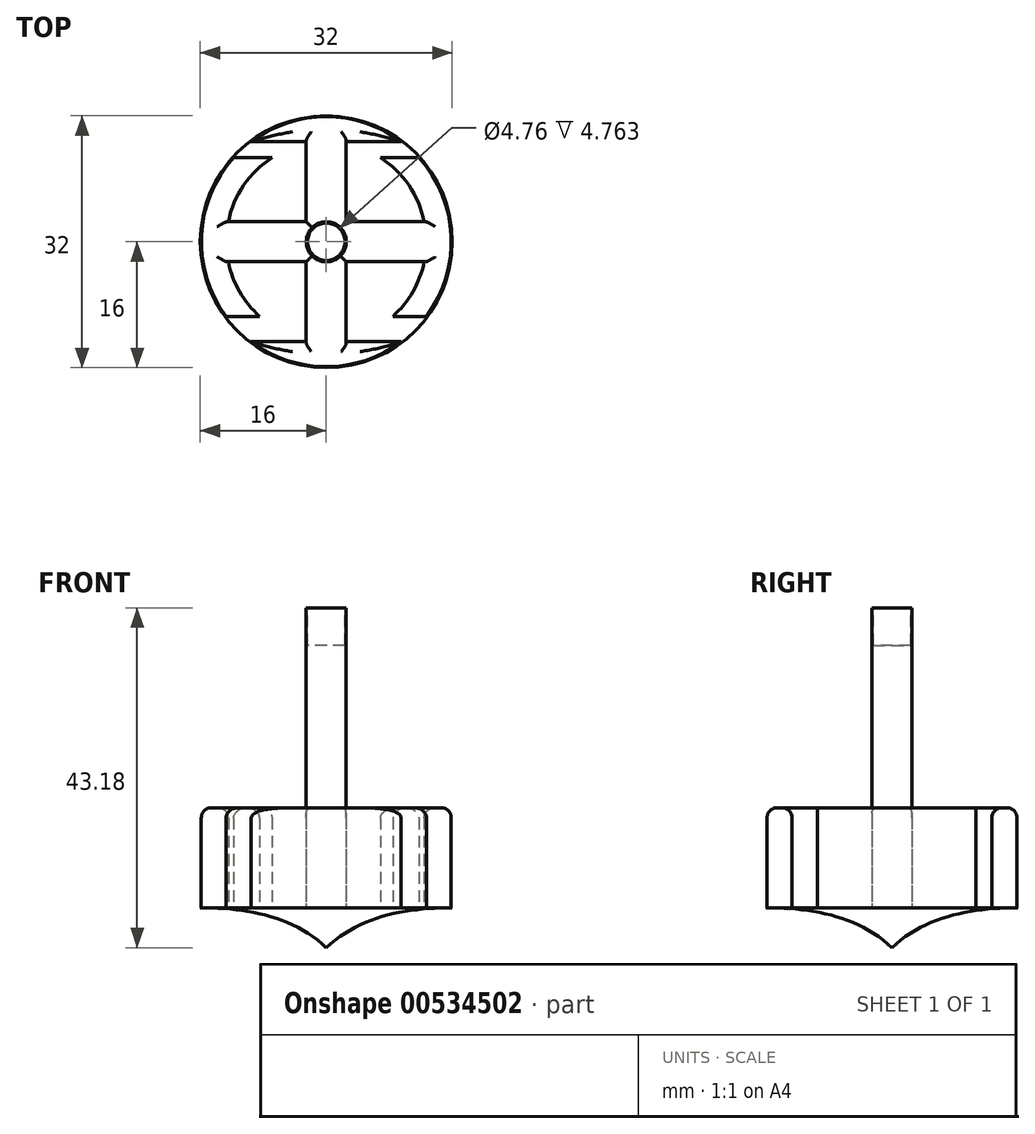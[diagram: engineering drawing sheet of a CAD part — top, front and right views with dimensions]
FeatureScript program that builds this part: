
annotation { "Feature Type Name" : "Feature", "Feature Type Description" : "" }
export const myFeature = defineFeature(function(context is Context, id is Id, definition is map)
    precondition{}
    {
        {
            var Q0;
            Q0=qCreatedBy(makeId("Top.planeOp"),FACE);
            var sketch = newSketch(context, id + "F0", { "sketchPlane" : qUnion([Q0])});
            skArc(sketch, "E0", {"start": v(-15.88, 0) * mm, "mid": v(-15.07, -5) * mm, "end": v(-12.73, -9.48) * mm});
            skArc(sketch, "E1", {"start": v(-15.88, 0) * mm, "mid": v(-14.8, 5.72) * mm, "end": v(-11.75, 10.67) * mm});
            skArc(sketch, "E2", {"start": v(15.88, 0) * mm, "mid": v(14.8, 5.72) * mm, "end": v(11.75, 10.67) * mm});
            skArc(sketch, "E3", {"start": v(15.88, 0) * mm, "mid": v(15.07, -5) * mm, "end": v(12.73, -9.48) * mm});
            skArc(sketch, "E4", {"start": v(-12.7, 0) * mm, "mid": v(-11.15, 6.08) * mm, "end": v(-6.89, 10.67) * mm});
            skArc(sketch, "E5", {"start": v(-12.7, 0) * mm, "mid": v(-11.59, -5.2) * mm, "end": v(-8.45, -9.48) * mm});
            skArc(sketch, "E6", {"start": v(12.7, 0) * mm, "mid": v(11.15, 6.08) * mm, "end": v(6.89, 10.67) * mm});
            skArc(sketch, "E7", {"start": v(12.7, 0) * mm, "mid": v(11.59, -5.2) * mm, "end": v(8.45, -9.48) * mm});
            skLineSegment(sketch, "E8", {"start": v(-11.75, 10.67) * mm, "end": v(-6.89, 10.67) * mm});
            skLineSegment(sketch, "E9", {"start": v(-8.45, -9.48) * mm, "end": v(-12.73, -9.48) * mm});
            skLineSegment(sketch, "E10", {"start": v(8.45, -9.48) * mm, "end": v(12.73, -9.48) * mm});
            skLineSegment(sketch, "E11", {"start": v(6.89, 10.67) * mm, "end": v(11.75, 10.67) * mm});
            skLineSegment(sketch, "E12", {"start": v(0, 12.7) * mm, "end": v(9.52, 12.7) * mm});
            skLineSegment(sketch, "E13", {"start": v(0, 12.7) * mm, "end": v(-9.52, 12.7) * mm});
            skArc(sketch, "E14", {"start": v(0, 15.88) * mm, "mid": v(-5.02, 15.06) * mm, "end": v(-9.52, 12.7) * mm});
            skArc(sketch, "E15", {"start": v(0, 15.88) * mm, "mid": v(5.02, 15.06) * mm, "end": v(9.53, 12.7) * mm});
            skLineSegment(sketch, "E16", {"start": v(0, -12.7) * mm, "end": v(9.52, -12.7) * mm});
            skLineSegment(sketch, "E17", {"start": v(0, -12.7) * mm, "end": v(-9.52, -12.7) * mm});
            skArc(sketch, "E18", {"start": v(0, -15.88) * mm, "mid": v(5.02, -15.06) * mm, "end": v(9.53, -12.7) * mm});
            skArc(sketch, "E19", {"start": v(0, -15.88) * mm, "mid": v(-5.02, -15.06) * mm, "end": v(-9.52, -12.7) * mm});
            skLineSegment(sketch, "E20", {"start": v(0, 2.54) * mm, "end": v(-2.54, 2.54) * mm});
            skLineSegment(sketch, "E21", {"start": v(0, -2.54) * mm, "end": v(-2.54, -2.54) * mm});
            skLineSegment(sketch, "E22", {"start": v(-2.54, -2.54) * mm, "end": v(-2.54, 0) * mm});
            skLineSegment(sketch, "E23", {"start": v(0, -2.54) * mm, "end": v(2.54, -2.54) * mm});
            skLineSegment(sketch, "E24", {"start": v(2.54, 0) * mm, "end": v(2.54, -2.54) * mm});
            skLineSegment(sketch, "E25", {"start": v(2.54, 0) * mm, "end": v(2.54, 2.54) * mm});
            skLineSegment(sketch, "E26", {"start": v(2.54, 2.54) * mm, "end": v(0, 2.54) * mm});
            skLineSegment(sketch, "E27", {"start": v(-2.54, 2.54) * mm, "end": v(-12.44, 2.54) * mm});
            skLineSegment(sketch, "E28", {"start": v(-2.54, 2.54) * mm, "end": v(-2.54, 12.7) * mm});
            skLineSegment(sketch, "E29", {"start": v(2.54, 2.54) * mm, "end": v(2.54, 12.7) * mm});
            skLineSegment(sketch, "E30", {"start": v(-2.54, -2.54) * mm, "end": v(-12.44, -2.54) * mm});
            skLineSegment(sketch, "E31", {"start": v(-2.54, -2.54) * mm, "end": v(-2.54, -12.7) * mm});
            skLineSegment(sketch, "E32", {"start": v(2.54, -2.54) * mm, "end": v(2.54, -12.7) * mm});
            skLineSegment(sketch, "E33", {"start": v(2.54, -2.54) * mm, "end": v(12.44, -2.54) * mm});
            skLineSegment(sketch, "E34", {"start": v(2.54, 2.54) * mm, "end": v(12.44, 2.54) * mm});
            skLineSegment(sketch, "E35", {"start": v(-2.54, 0) * mm, "end": v(-2.54, 2.54) * mm});
            skSolve(sketch);
        }
        {
            var Q0;
            Q0 = qSketchRegion(id + "F0", true);
            extrude(context, id + "F1", {"entities" : qUnion([Q0]), "depth" : 12.7 * mm, "offsetDistance" : 25.4 * mm});
        }
        {
            var Q0;
            Q0=makeQuery(id+"F1.opExtrude","CAP_FACE",FACE,{"disambiguationData":[OSD([sQuery(id+"F0.wireOp",EDGE,"4Uun5BIm-TfXw-1pBh-UEKI-oQnObC4pccgt"),sQuery(id+"F0.wireOp",EDGE,"Lj9ukLqR-FDjl-bsbc-OOmQ-CZc7TmuNFC0M"),sQuery(id+"F0.wireOp",EDGE,"VEHvtU8j-b5D7-3D3Z-QU2X-H6E8UUCLkPfg"),sQuery(id+"F0.wireOp",EDGE,"fTyzN8CT-LdRs-CvbE-Hdes-9KVt6GUuwTxW"),sQuery(id+"F0.wireOp",EDGE,"xC0Xyikr-JMaQ-RKEJ-MLoV-DoZoL4MRR0Z7"),sQuery(id+"F0.wireOp",EDGE,"O77jC6HB-1WUQ-Wr5y-nwV6-KnxJamGugmHo"),sQuery(id+"F0.wireOp",EDGE,"fKrxIogu-vjJD-mybC-vPzq-i7p9JX8OsxXe"),sQuery(id+"F0.wireOp",EDGE,"VRdrLMRh-709r-ll4j-uTnO-MFjaDkaupSMg"),sQuery(id+"F0.wireOp",EDGE,"E0"),sQuery(id+"F0.wireOp",EDGE,"E1"),sQuery(id+"F0.wireOp",EDGE,"E2"),sQuery(id+"F0.wireOp",EDGE,"E3"),sQuery(id+"F0.wireOp",EDGE,"E4"),sQuery(id+"F0.wireOp",EDGE,"E5"),sQuery(id+"F0.wireOp",EDGE,"E6"),sQuery(id+"F0.wireOp",EDGE,"E7"),sQuery(id+"F0.wireOp",EDGE,"E8"),sQuery(id+"F0.wireOp",EDGE,"E9"),sQuery(id+"F0.wireOp",EDGE,"E10"),sQuery(id+"F0.wireOp",EDGE,"E11"),sQuery(id+"F0.wireOp",EDGE,"E12"),sQuery(id+"F0.wireOp",EDGE,"E13"),sQuery(id+"F0.wireOp",EDGE,"E14"),sQuery(id+"F0.wireOp",EDGE,"E15"),sQuery(id+"F0.wireOp",EDGE,"E16"),sQuery(id+"F0.wireOp",EDGE,"E17"),sQuery(id+"F0.wireOp",EDGE,"E18"),sQuery(id+"F0.wireOp",EDGE,"E19")])],"isStart":false});
            var sketch = newSketch(context, id + "F2", { "sketchPlane" : qUnion([Q0])});
            skCircle(sketch, "E36", {"center": v(0, 0) * mm, "radius": 2.54 * mm});
            skSolve(sketch);
        }
        {
            var Q0;
            Q0=makeQuery(id+"F2.imprint","IMPRINT",FACE,{"disambiguationData":[TD([[makeQuery(id+"F2.imprint","IMPRINT",EDGE,{"derivedFrom":sQuery(id+"F2.wireOp",EDGE,"E36")}),1.0]])]});
            extrude(context, id + "F3", {"entities" : qUnion([Q0]), "depth" : 25.4 * mm, "offsetDistance" : 25.4 * mm});
        }
        {
            var Q0;
            Q0=makeQuery(id+"F3.opExtrude","CAP_FACE",FACE,{"disambiguationData":[OSD([sQuery(id+"F2.wireOp",EDGE,"E36")])],"isStart":false});
            var sketch = newSketch(context, id + "F4", { "sketchPlane" : qUnion([Q0])});
            skCircle(sketch, "E37", {"center": v(0, 0) * mm, "radius": 2.38 * mm});
            skSolve(sketch);
        }
        {
            var Q0;
            Q0=makeQuery(id+"F4.imprint","IMPRINT",FACE,{"disambiguationData":[TD([[makeQuery(id+"F4.imprint","IMPRINT",EDGE,{"derivedFrom":sQuery(id+"F4.wireOp",EDGE,"E37")}),1.0]])]});
            extrude(context, id + "F5", {"entities" : qUnion([Q0]), "operationType" : NewBodyOperationType.REMOVE, "oppositeDirection" : true, "depth" : 4.76 * mm, "offsetDistance" : 25.4 * mm});
        }
        {
            var Q0;
            Q0=qCreatedBy(makeId("Front.planeOp"),FACE);
            var sketch = newSketch(context, id + "F6", { "sketchPlane" : qUnion([Q0])});
            skLineSegment(sketch, "E38", {"start": v(0, 0) * mm, "end": v(0, -5.08) * mm});
            skFitSpline(sketch, "E39", {"points": [v(0, -5.08) * mm, v(16, 0) * mm], "startDerivative": vector(12.73, 12.11) * mm, "endDerivative": vector(17.14, 0) * mm});
            skLineSegment(sketch, "E40", {"start": v(0, 0) * mm, "end": v(16, 0) * mm});
            skSolve(sketch);
        }
        {
            var Q0;
            Q0=makeQuery(id+"F6.imprint","IMPRINT",FACE,{"disambiguationData":[TD([[makeQuery(id+"F6.imprint","IMPRINT",EDGE,{"derivedFrom":sQuery(id+"F6.wireOp",EDGE,"E38")}),1.0]])]});
            var Q1;
            Q1=sQuery(id+"F6.wireOp",EDGE,"E38");
            revolve(context, id + "F7", {"operationType" : NewBodyOperationType.ADD, "entities" : qUnion([Q0]), "axis" : qUnion([Q1]), "revolveType" : RevolveType.FULL});
        }
        {
            var Q0;
            Q0=makeQuery(id+"F1.opExtrude","CAP_EDGE",EDGE,{"disambiguationData":[OSD([sQuery(id+"F0.wireOp",EDGE,"E32")])],"isStart":false});
            var Q1;
            Q1=makeQuery(id+"F1.opExtrude","CAP_EDGE",EDGE,{"disambiguationData":[OSD([sQuery(id+"F0.wireOp",EDGE,"E31")])],"isStart":false});
            var Q2;
            Q2=makeQuery(id+"F1.opExtrude","CAP_EDGE",EDGE,{"disambiguationData":[OSD([sQuery(id+"F0.wireOp",EDGE,"E30")])],"isStart":false});
            var Q3;
            Q3=makeQuery(id+"F1.opExtrude","CAP_EDGE",EDGE,{"disambiguationData":[OSD([sQuery(id+"F0.wireOp",EDGE,"E27")])],"isStart":false});
            var Q4;
            Q4=makeQuery(id+"F1.opExtrude","CAP_EDGE",EDGE,{"disambiguationData":[OSD([sQuery(id+"F0.wireOp",EDGE,"E28")])],"isStart":false});
            var Q5;
            Q5=makeQuery(id+"F1.opExtrude","CAP_EDGE",EDGE,{"disambiguationData":[OSD([sQuery(id+"F0.wireOp",EDGE,"E29")])],"isStart":false});
            var Q6;
            Q6=makeQuery(id+"F1.opExtrude","CAP_EDGE",EDGE,{"disambiguationData":[OSD([sQuery(id+"F0.wireOp",EDGE,"E34")])],"isStart":false});
            var Q7;
            Q7=makeQuery(id+"F1.opExtrude","CAP_EDGE",EDGE,{"disambiguationData":[OSD([sQuery(id+"F0.wireOp",EDGE,"E33")])],"isStart":false});
            fillet(context, id + "F8", {"entities" : qUnion([Q0, Q1, Q2, Q3, Q4, Q5, Q6, Q7]), "radius" : 0.64 * mm, "tangentPropagation" : true, "allowEdgeOverflow" : false});
        }
        {
            var Q0;
            Q0=makeQuery(id+"F1.opExtrude","CAP_EDGE",EDGE,{"disambiguationData":[OSD([sQuery(id+"F0.wireOp",EDGE,"E18"),sQuery(id+"F0.wireOp",EDGE,"E19")])],"isStart":false});
            var Q1;
            Q1=makeQuery(id+"F1.opExtrude","CAP_EDGE",EDGE,{"disambiguationData":[OSD([sQuery(id+"F0.wireOp",EDGE,"E2"),sQuery(id+"F0.wireOp",EDGE,"E3")])],"isStart":false});
            var Q2;
            Q2=makeQuery(id+"F1.opExtrude","CAP_EDGE",EDGE,{"disambiguationData":[OSD([sQuery(id+"F0.wireOp",EDGE,"E14"),sQuery(id+"F0.wireOp",EDGE,"E15")])],"isStart":false});
            var Q3;
            Q3=makeQuery(id+"F1.opExtrude","CAP_EDGE",EDGE,{"disambiguationData":[OSD([sQuery(id+"F0.wireOp",EDGE,"E0"),sQuery(id+"F0.wireOp",EDGE,"E1")])],"isStart":false});
            var Q4;
            Q4=makeQuery(id+"F1.opExtrude","CAP_EDGE",EDGE,{"disambiguationData":[OSD([sQuery(id+"F0.wireOp",EDGE,"E7")])],"isStart":false});
            var Q5;
            Q5=makeQuery(id+"F1.opExtrude","CAP_EDGE",EDGE,{"disambiguationData":[OSD([sQuery(id+"F0.wireOp",EDGE,"E6")])],"isStart":false});
            var Q6;
            Q6=makeQuery(id+"F1.opExtrude","CAP_EDGE",EDGE,{"disambiguationData":[OSD([sQuery(id+"F0.wireOp",EDGE,"E12")])],"isStart":false});
            var Q7;
            Q7=makeQuery(id+"F1.opExtrude","CAP_EDGE",EDGE,{"disambiguationData":[OSD([sQuery(id+"F0.wireOp",EDGE,"E4")])],"isStart":false});
            var Q8;
            Q8=makeQuery(id+"F1.opExtrude","CAP_EDGE",EDGE,{"disambiguationData":[OSD([sQuery(id+"F0.wireOp",EDGE,"E5")])],"isStart":false});
            var Q9;
            Q9=makeQuery(id+"F1.opExtrude","CAP_EDGE",EDGE,{"disambiguationData":[OSD([sQuery(id+"F0.wireOp",EDGE,"E17")])],"isStart":false});
            var Q10;
            Q10=makeQuery(id+"F1.opExtrude","CAP_EDGE",EDGE,{"disambiguationData":[OSD([sQuery(id+"F0.wireOp",EDGE,"E16")])],"isStart":false});
            var Q11;
            Q11=makeQuery(id+"F1.opExtrude","CAP_EDGE",EDGE,{"disambiguationData":[OSD([sQuery(id+"F0.wireOp",EDGE,"E13")])],"isStart":false});
            fillet(context, id + "F9", {"entities" : qUnion([Q0, Q1, Q2, Q3, Q4, Q5, Q6, Q7, Q8, Q9, Q10, Q11]), "radius" : 1.27 * mm, "tangentPropagation" : true, "allowEdgeOverflow" : false});
        }
    });
